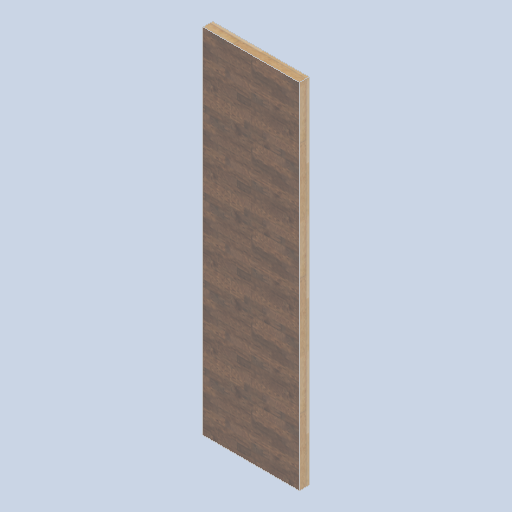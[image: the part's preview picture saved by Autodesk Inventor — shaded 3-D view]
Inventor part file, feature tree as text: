
AUTODESK INVENTOR PART (.ipt)
format: ipt  version: 2024.2 (Build 282272000, 272)  size: 163,328 bytes
history: native  units: in
note: dims shown in document units (in); Inventor stores cm internally (conversion verified against a paired STEP export)
features: other x3, sketch x1
ambient origin geometry x8: Origin, YZ Plane, XZ Plane, XY Plane, X Axis, Y Axis, Z Axis, Center Point
bodies: Solid1 (feature_tree)
feature tree (4):
  other  "front_wall_block04.ipt"
  other  "Solid1::front_wall_block04.ipt"
  other  "TaggingFeature1"
  sketch  "Sketch1"  dims[d0=0.3937in]
